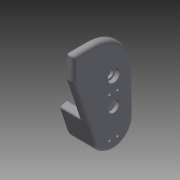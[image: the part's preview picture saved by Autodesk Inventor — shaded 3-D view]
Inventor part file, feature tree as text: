
AUTODESK INVENTOR PART (.ipt)
format: ipt  version: 2015 (Build 190159000, 159)  size: 271,360 bytes
history: native  units: mm
features: extrude x8, sketch x8, fillet x4
ambient origin geometry x8: Origin, YZ Plane, XZ Plane, XY Plane, X Axis, Y Axis, Z Axis, Center Point
bodies: Solid1 (feature_tree)
feature tree (20):
  extrude  "Extrusion1"  Depth=66.3mm
  extrude  "Extrusion2"  Depth=55.0mm
  extrude  "Extrusion3"  Depth=55.0mm
  extrude  "Extrusion4"  Depth=9.9mm
  extrude  "Extrusion5"  Depth=9.9mm
  extrude  "Extrusion6"  Depth=3.0mm
  extrude  "Extrusion7"  Depth=3.0mm
  fillet  "Fillet1"  Radius=3.0mm
  extrude  "Extrusion8"  Depth=25.0mm
  fillet  "Fillet2"  Radius=45.0mm
  fillet  "Fillet3"  Radius=15.0mm
  fillet  "Fillet4"  Radius=5.0mm
  sketch  "Sketch1"  dims[d0=33.15mm d2=66.3mm]
  sketch  "Sketch2"  dims[d4=18.1mm d5=55.0mm]
  sketch  "Sketch3"  dims[d6=20.0mm d7=55.0mm]
  sketch  "Sketch4"  dims[d8=40.2mm d9=9.9mm]
  sketch  "Sketch5"  dims[d10=9.5mm d11=9.9mm]
  sketch  "Sketch6"  dims[d12=9.5mm d13=3.0mm]
  sketch  "Sketch7"  dims[d14=3.0mm d15=3.0mm d16=3.0mm]
  sketch  "Sketch8"  dims[d17=13.6mm d20=25.0mm d21=45.0mm d22=15.0mm d23=5.0mm d24=0.0mm d25=5.0mm d26=0.0mm d27=25.0mm d28=28.0mm d29=5.0mm d30=0.0mm d31=3.0mm d32=0.0mm d33=40.5mm d34=20.0mm d35=3.0mm d36=0.0mm d37=1.0mm d38=0.0mm d39=10.0mm d40=3.0mm d41=0.0mm d42=1.0mm d43=54.0mm d44=10.0mm d45=10.0mm d46=25.9mm d47=0.0mm d48=4.0mm d49=2.0mm d50=2.0mm]
